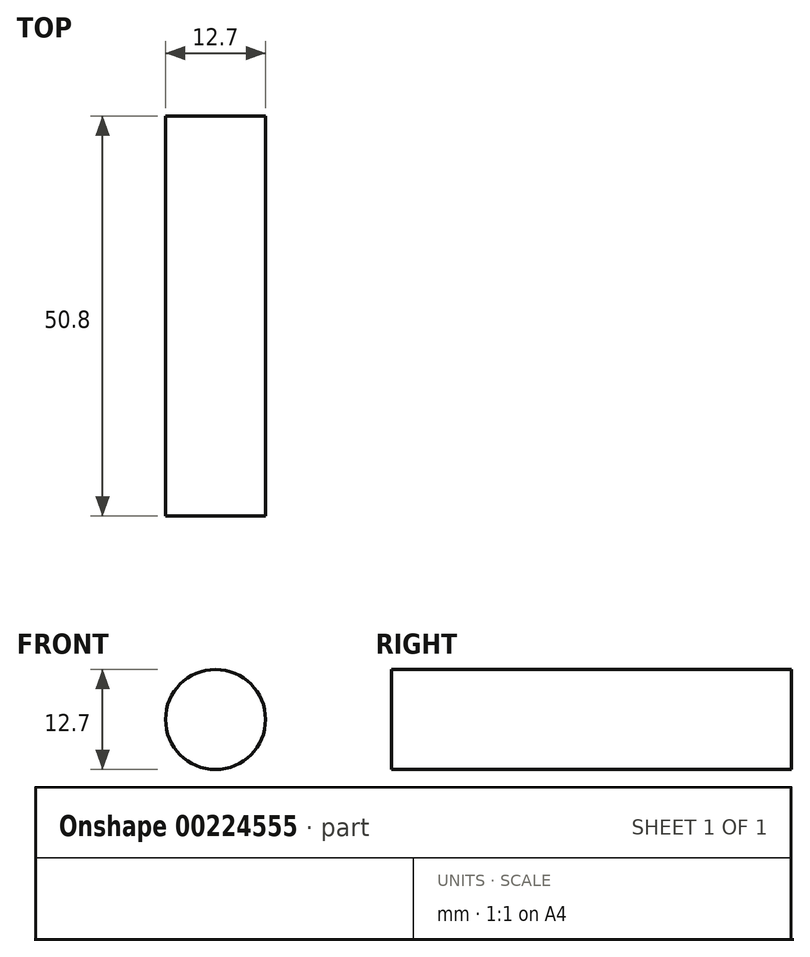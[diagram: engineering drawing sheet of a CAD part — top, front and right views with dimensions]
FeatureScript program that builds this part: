
annotation { "Feature Type Name" : "Feature", "Feature Type Description" : "" }
export const myFeature = defineFeature(function(context is Context, id is Id, definition is map)
    precondition{}
    {
        {
            var Q0;
            Q0=qCreatedBy(makeId("Front.planeOp"),FACE);
            var sketch = newSketch(context, id + "F0", { "sketchPlane" : qUnion([Q0])});
            skCircle(sketch, "E0", {"center": v(-35.5, 26.5) * mm, "radius": 6.35 * mm});
            skSolve(sketch);
        }
        {
            var Q0;
            Q0=makeQuery(id+"F0.imprint","IMPRINT",FACE,{"disambiguationData":[TD([[makeQuery(id+"F0.imprint","IMPRINT",EDGE,{"derivedFrom":sQuery(id+"F0.wireOp",EDGE,"E0")}),1.0]])]});
            extrude(context, id + "F1", {"entities" : qUnion([Q0]), "depth" : 50.8 * mm});
        }
    });
